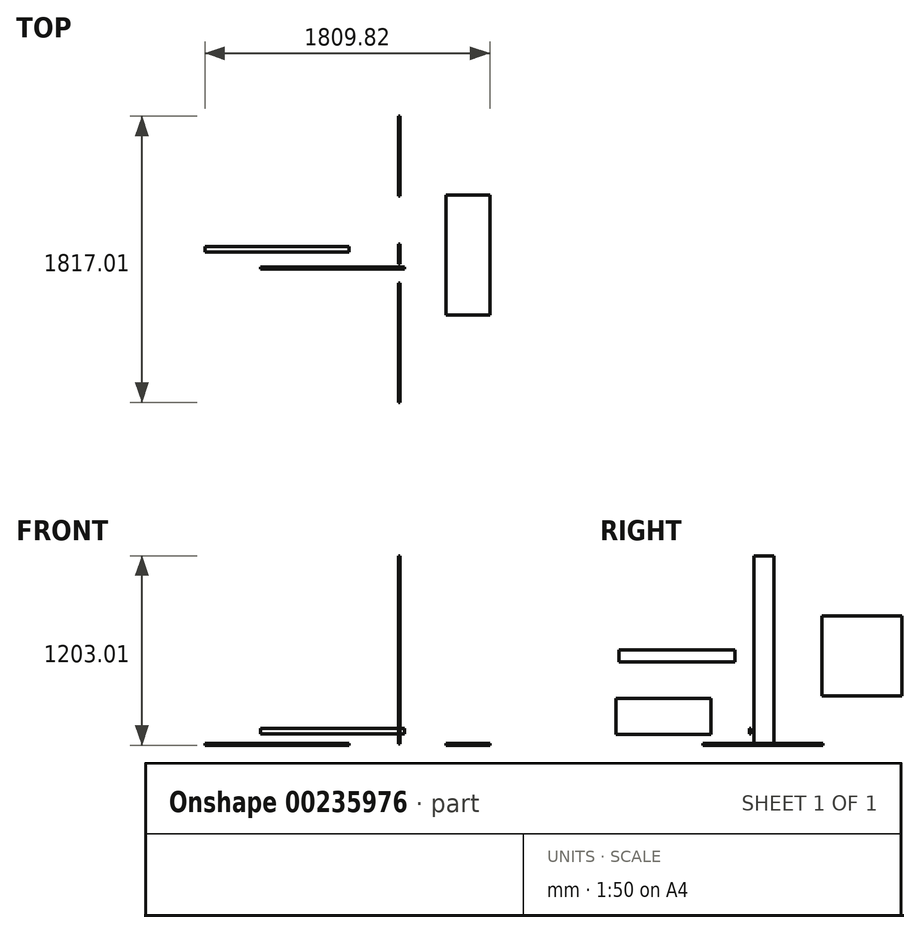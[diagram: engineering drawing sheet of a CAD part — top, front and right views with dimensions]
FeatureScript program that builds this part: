
annotation { "Feature Type Name" : "Feature", "Feature Type Description" : "" }
export const myFeature = defineFeature(function(context is Context, id is Id, definition is map)
    precondition{}
    {
        {
            var Q0;
            Q0=qCreatedBy(makeId("Right.planeOp"),FACE);
            var sketch = newSketch(context, id + "F0", { "sketchPlane" : qUnion([Q0])});
            skLineSegment(sketch, "E0.bottom", {"start": v(18.41, 9.2) * mm, "end": v(145.41, 9.2) * mm});
            skLineSegment(sketch, "E0.top", {"start": v(18.41, 1203) * mm, "end": v(145.41, 1203) * mm});
            skLineSegment(sketch, "E0.left", {"start": v(18.41, 9.2) * mm, "end": v(18.41, 1203) * mm});
            skLineSegment(sketch, "E0.right", {"start": v(145.41, 9.2) * mm, "end": v(145.41, 1203) * mm});
            skSolve(sketch);
        }
        {
            var Q0;
            Q0 = qSketchRegion(id + "F0", true);
            extrude(context, id + "F1", {"entities" : qUnion([Q0]), "depth" : 11.1 * mm});
        }
        {
            var Q0;
            Q0=qCreatedBy(makeId("Right.planeOp"),FACE);
            var sketch = newSketch(context, id + "F2", { "sketchPlane" : qUnion([Q0])});
            skLineSegment(sketch, "E1.bottom", {"start": v(-859.1, 296.4) * mm, "end": v(-255.84, 296.4) * mm});
            skLineSegment(sketch, "E1.top", {"start": v(-859.1, 67.8) * mm, "end": v(-255.84, 67.8) * mm});
            skLineSegment(sketch, "E1.left", {"start": v(-859.1, 296.4) * mm, "end": v(-859.1, 67.8) * mm});
            skLineSegment(sketch, "E1.right", {"start": v(-255.84, 296.4) * mm, "end": v(-255.84, 67.8) * mm});
            skSolve(sketch);
        }
        {
            var Q0;
            Q0 = qSketchRegion(id + "F2", true);
            extrude(context, id + "F3", {"entities" : qUnion([Q0]), "depth" : 11.1 * mm});
        }
        {
            var Q0;
            Q0=qCreatedBy(makeId("Right.planeOp"),FACE);
            var sketch = newSketch(context, id + "F4", { "sketchPlane" : qUnion([Q0])});
            skLineSegment(sketch, "E2.bottom", {"start": v(-837.82, 528.86) * mm, "end": v(-101.22, 528.86) * mm});
            skLineSegment(sketch, "E2.top", {"start": v(-837.82, 605.06) * mm, "end": v(-101.22, 605.06) * mm});
            skLineSegment(sketch, "E2.left", {"start": v(-837.82, 528.86) * mm, "end": v(-837.82, 605.06) * mm});
            skLineSegment(sketch, "E2.right", {"start": v(-101.22, 528.86) * mm, "end": v(-101.22, 605.06) * mm});
            skSolve(sketch);
        }
        {
            var Q0;
            Q0 = qSketchRegion(id + "F4", true);
            extrude(context, id + "F5", {"entities" : qUnion([Q0]), "depth" : 11.1 * mm});
        }
        {
            var Q0;
            Q0=qCreatedBy(makeId("Top.planeOp"),FACE);
            var sketch = newSketch(context, id + "F6", { "sketchPlane" : qUnion([Q0])});
            skLineSegment(sketch, "E3.bottom", {"start": v(301.35, -305.6) * mm, "end": v(580.75, -305.6) * mm});
            skLineSegment(sketch, "E3.top", {"start": v(301.35, 456.4) * mm, "end": v(580.75, 456.4) * mm});
            skLineSegment(sketch, "E3.left", {"start": v(301.35, -305.6) * mm, "end": v(301.35, 456.4) * mm});
            skLineSegment(sketch, "E3.right", {"start": v(580.75, -305.6) * mm, "end": v(580.75, 456.4) * mm});
            skSolve(sketch);
        }
        {
            var Q0;
            Q0 = qSketchRegion(id + "F6", true);
            extrude(context, id + "F7", {"entities" : qUnion([Q0]), "depth" : 11.1 * mm});
        }
        {
            var Q0;
            Q0=qCreatedBy(makeId("Right.planeOp"),FACE);
            var sketch = newSketch(context, id + "F8", { "sketchPlane" : qUnion([Q0])});
            skLineSegment(sketch, "E4.bottom", {"start": v(449.92, 821.96) * mm, "end": v(957.92, 821.96) * mm});
            skLineSegment(sketch, "E4.top", {"start": v(449.92, 313.96) * mm, "end": v(957.92, 313.96) * mm});
            skLineSegment(sketch, "E4.left", {"start": v(449.92, 821.96) * mm, "end": v(449.92, 313.96) * mm});
            skLineSegment(sketch, "E4.right", {"start": v(957.92, 821.96) * mm, "end": v(957.92, 313.96) * mm});
            skSolve(sketch);
        }
        {
            var Q0;
            Q0 = qSketchRegion(id + "F8", true);
            extrude(context, id + "F9", {"entities" : qUnion([Q0]), "depth" : 11.1 * mm});
        }
        {
            var Q0;
            Q0=qCreatedBy(makeId("Front.planeOp"),FACE);
            var sketch = newSketch(context, id + "F10", { "sketchPlane" : qUnion([Q0])});
            skLineSegment(sketch, "E5.bottom", {"start": v(-875.98, 70.9) * mm, "end": v(38.42, 70.9) * mm});
            skLineSegment(sketch, "E5.top", {"start": v(-875.98, 105.83) * mm, "end": v(38.42, 105.83) * mm});
            skLineSegment(sketch, "E5.left", {"start": v(-875.98, 70.9) * mm, "end": v(-875.98, 105.83) * mm});
            skLineSegment(sketch, "E5.right", {"start": v(38.42, 70.9) * mm, "end": v(38.42, 105.83) * mm});
            skSolve(sketch);
        }
        {
            var Q0;
            Q0 = qSketchRegion(id + "F10", true);
            extrude(context, id + "F11", {"entities" : qUnion([Q0]), "depth" : 11.1 * mm});
        }
        {
            var Q0;
            Q0=qCreatedBy(makeId("Top.planeOp"),FACE);
            var sketch = newSketch(context, id + "F12", { "sketchPlane" : qUnion([Q0])});
            skLineSegment(sketch, "E6.bottom", {"start": v(-1229.07, 129.77) * mm, "end": v(-314.67, 129.77) * mm});
            skLineSegment(sketch, "E6.top", {"start": v(-1229.07, 94.84) * mm, "end": v(-314.67, 94.84) * mm});
            skLineSegment(sketch, "E6.left", {"start": v(-1229.07, 129.77) * mm, "end": v(-1229.07, 94.84) * mm});
            skLineSegment(sketch, "E6.right", {"start": v(-314.67, 129.77) * mm, "end": v(-314.67, 94.84) * mm});
            skSolve(sketch);
        }
        {
            var Q0;
            Q0 = qSketchRegion(id + "F12", true);
            extrude(context, id + "F13", {"entities" : qUnion([Q0]), "depth" : 11.1 * mm});
        }
    });
